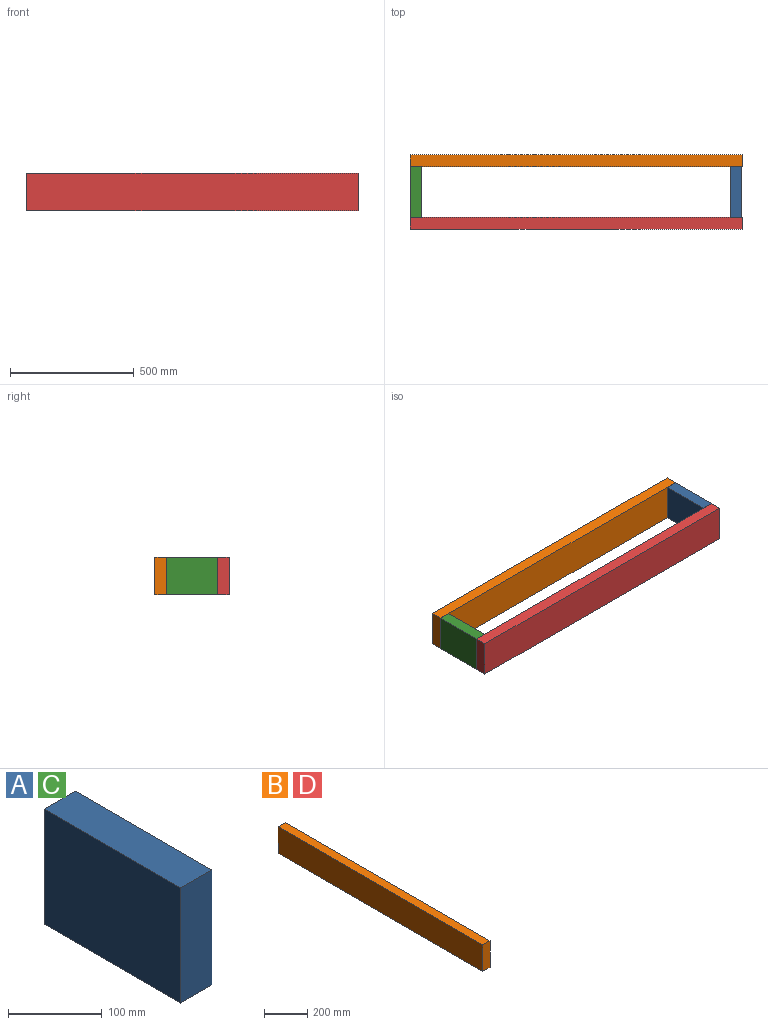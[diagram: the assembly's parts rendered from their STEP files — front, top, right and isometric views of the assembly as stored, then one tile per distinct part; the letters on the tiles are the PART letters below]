
ASSEMBLY  parts=4 mates=9
PART A: 6 faces, bbox 47x206x150 mm
  f0: plane 206x47mm, normal (0,0,-1), area 9682mm2, adj f1,f3,f4,f5
  f1: plane 206x150mm, normal (1,0,0), area 30900mm2, adj f0,f2,f4,f5
  f2: plane 206x47mm, normal (0,0,1), area 9682mm2, adj f1,f3,f4,f5
  f3: plane 206x150mm, normal (-1,0,0), area 30900mm2, adj f0,f2,f4,f5
  f4: plane 150x47mm, normal (0,-1,0), area 7050mm2, adj f0,f1,f2,f3
  f5: plane 150x47mm, normal (0,1,0), area 7050mm2, adj f0,f1,f2,f3
PART B: 6 faces, bbox 47x1340x150 mm
  f0: plane 1340x47mm, normal (0,0,-1), area 62980mm2, adj f1,f3,f4,f5
  f1: plane 1340x150mm, normal (1,0,0), area 201000mm2, adj f0,f2,f4,f5
  f2: plane 1340x47mm, normal (0,0,1), area 62980mm2, adj f1,f3,f4,f5
  f3: plane 1340x150mm, normal (-1,0,0), area 201000mm2, adj f0,f2,f4,f5
  f4: plane 150x47mm, normal (0,-1,0), area 7050mm2, adj f0,f1,f2,f3
  f5: plane 150x47mm, normal (0,1,0), area 7050mm2, adj f0,f1,f2,f3
PART C: same geometry as A
PART D: same geometry as B
PLACE A t=(1293,0,0)mm
PLACE B rot(axis=(0,0,1),90deg) t=(-23.5,23.5,0)mm
PLACE C at identity fixed
PLACE D rot(axis=(-0.71,-0.71,0),180deg) t=(1316.5,-229.5,0)mm
MATE planar C.f3 <-> D.f4  axis (-1,0,0) through (-23.5,-103,0)mm
MATE planar C.f4 <-> A.f4  axis (0,-1,0) through (0,-206,0)mm
MATE planar C.f2 <-> A.f2  axis (0,0,1) through (0,-103,75)mm
MATE planar D.f0 <-> A.f2  axis (0,0,1) through (646.5,-229.5,75)mm
MATE planar D.f1 <-> A.f4  axis (0,1,0) through (646.5,-206,0)mm
MATE planar B.f3 <-> A.f5  axis (0,-1,0) through (646.5,0,0)mm
MATE planar D.f5 <-> A.f1  axis (1,0,0) through (1316.5,-229.5,0)mm
MATE planar B.f4 <-> A.f1  axis (1,0,0) through (1316.5,23.5,0)mm
MATE planar B.f2 <-> A.f2  axis (0,0,1) through (646.5,23.5,75)mm
